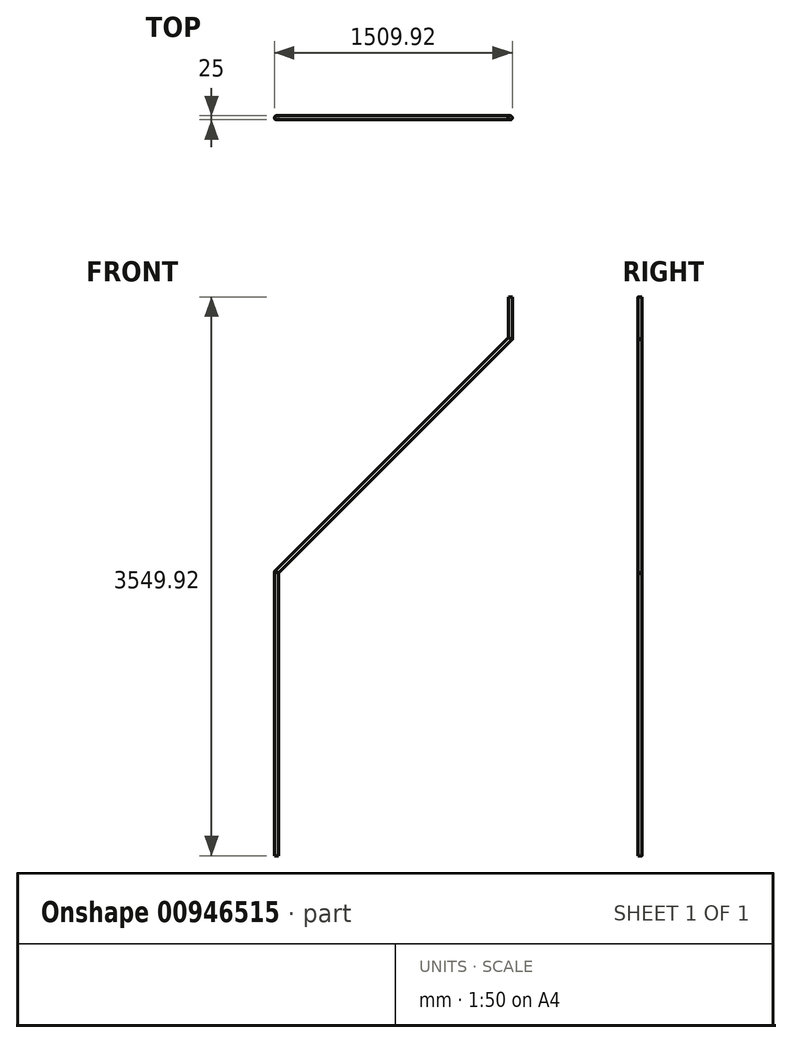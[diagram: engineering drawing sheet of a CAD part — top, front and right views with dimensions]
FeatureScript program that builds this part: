
annotation { "Feature Type Name" : "Feature", "Feature Type Description" : "" }
export const myFeature = defineFeature(function(context is Context, id is Id, definition is map)
    precondition{}
    {
        {
            var Q0;
            Q0=qCreatedBy(makeId("Front.planeOp"),FACE);
            var sketch = newSketch(context, id + "F0", { "sketchPlane" : qUnion([Q0])});
            skLineSegment(sketch, "E0", {"start": v(0, 0) * mm, "end": v(0, 1600) * mm});
            skLineSegment(sketch, "E1", {"start": v(0, 1600) * mm, "end": v(0, 1800) * mm});
            skLineSegment(sketch, "E2", {"start": v(0, 1800) * mm, "end": v(1484.92, 3284.92) * mm});
            skLineSegment(sketch, "E3", {"start": v(1484.92, 3284.92) * mm, "end": v(1484.92, 3549.92) * mm});
            skLineSegment(sketch, "E4", {"start": v(0, 1800) * mm, "end": v(2377.2, 1800) * mm, "construction": true});
            skSolve(sketch);
        }
        {
            var Q0;
            Q0=qCreatedBy(makeId("Top.planeOp"),FACE);
            var sketch = newSketch(context, id + "F1", { "sketchPlane" : qUnion([Q0])});
            skCircle(sketch, "E5", {"center": v(0, 0) * mm, "radius": 12.5 * mm});
            skSolve(sketch);
        }
        {
            var Q0;
            Q0=makeQuery(id+"F1.imprint","IMPRINT",FACE,{"disambiguationData":[TD([[makeQuery(id+"F1.imprint","IMPRINT",EDGE,{"derivedFrom":sQuery(id+"F1.wireOp",EDGE,"E5")}),1.0]])]});
            var Q1;
            Q1=sQuery(id+"F0.wireOp",EDGE,"E0");
            var Q2;
            Q2=sQuery(id+"F0.wireOp",EDGE,"E1");
            var Q3;
            Q3=sQuery(id+"F0.wireOp",EDGE,"E2");
            var Q4;
            Q4=sQuery(id+"F0.wireOp",EDGE,"E3");
            sweep(context, id + "F2", {"profiles" : qUnion([Q0]), "path" : qUnion([Q1, Q2, Q3, Q4])});
        }
        {
            var Q0;
            Q0=makeQuery(id+"F2.opSweep","MID_CAP_EDGE",EDGE,{"disambiguationData":[OSD([sQuery(id+"F0.wireOp",VERTEX,"E2.start"),sQuery(id+"F1.wireOp",EDGE,"E5")])],"capPos":2.0});
            fillet(context, id + "F3", {"entities" : qUnion([Q0]), "radius" : 5 * mm, "tangentPropagation" : true, "allowEdgeOverflow" : false});
        }
        {
            var Q0;
            Q0=makeQuery(id+"F2.opSweep","MID_CAP_EDGE",EDGE,{"disambiguationData":[OSD([sQuery(id+"F0.wireOp",VERTEX,"E3.start"),sQuery(id+"F1.wireOp",EDGE,"E5")])],"capPos":3.0});
            fillet(context, id + "F4", {"entities" : qUnion([Q0]), "radius" : 5 * mm, "tangentPropagation" : true, "allowEdgeOverflow" : false});
        }
    });
